# Revit family: NBS_HeatraeSadia_DrctHotWtrStrgCylndrsDblFeed_MEGAFLOEcoSolarReadyDirect
name_source: partatom
category: Mechanical Equipment
revit_build: Autodesk Revit 2014 (Build: 20130709_2115(x64)
units: mm (PartAtom-declared; Revit-internal decimal feet)

## types (1)
- 260DD
    AssetType = Fixed
    BIMObjectName = NBS_HeatraeSadia_IndirectHotWaterStorageCylindersDoubleFeed_MEGAFLOEcoSolarReady-260DD
    BackUpElementControlHousingHeight = 1165 mm
    Color = White
    Connections = 22 mm compression fittings
    ControlHousingMaterial = NBS_Concept
    CylinderMaterial = NBS_Concept
    Description = Unvented direct hot water cylinder
    DurationUnit = year
    EffectiveCapacity = 0 m³
    ElectricalDeviceNominalPower = 0
    ElementControlHousingHeight = 916 mm  [stored 3.00525 ft]
    ErPRating = C
    Features = Extrernal expansion vessel, specially designed solar coil for maximum effeciency, sized to deliver hot water even when solar gain is low,
    FirstCurvatureRadius = 0 mm  [stored 0 ft]
    Fixing = Floor fixed
    FlowRate = ≤70 L/min
    HasProtectiveEarth = No
    HeatUpTime = 60 minutes (minimum)
    Height = 1798 mm  [stored 5.89895 ft]
    IfcExportAs = IfcTankType
    IfcExportType = STORAGE
    ImmersionHeater = Two 3 kW titanium elements with integral thermostat and thermal cut-out
    ManufacturerName = Heatrae Sadia
    ManufacturerURL = www.heatraesadia.com
    Material = Outer casing: Plastic-coated corrosion-proofed steel; Water container: Duplex stainless steel
    MaterialThickness = 0 mm  [stored 0 ft]
    ModelNumber = 95:050:508
    ModelReference = MEGAFLO Eco SolarReady - 260DD
    NBSCertification = http://www.nationalbimlibrary.com
    NBSDescription = Indirect hot water storage cylinders, double feed
    NBSReference = 90-15-35/350
    Name = IndirectHotWaterStorageCylindersDoubleFeed_MEGAFLOEcoSolarReady-260DD_HeatraeSadia
    NominalCapacity = 7.36 m³
    NominalCurrent = 0
    NominalDepth = 1909 mm
    NominalFrequencyRange = 50.0, 60.0
    NominalLengthOrDiameter = 579 mm
    NominalVoltage = 230.0, 240.0
    NominalWidthOrDiameter = 579 mm
    NumberOfPoles = 0
    OperatingWeight = 307.3
    OutletTemperatureRange = ≤60°C
    PatternType = Vertical cylinder
    PhaseAngle = 0.00°
    ProductInformation = www.heatraesadia.com/docs/Megaflo_Eco_SolaReady_Technical_Data.pdf
    SafetyFeatures = Manually resettable thermal cutout on electrical supply to solar differential controller, manually resettable cut-out on each heating element set to operate at 85°C, temperature and pressure relief valve factory set to operate at 10 bar and 90°C, factory-fitted thermal cut-out for integration into a solar circuit
    SecondCurvatureRadius = 0 mm  [stored 0 ft]
    Shape = Cylinder
    Size = 1909 x 780 x 780 mm
    SolarCoilSurfaceArea = 1.1 m²
    SolarCoilType = 25 mm diameter stainless steel
    SupplyPressureRange = 1.5-16.0 bar
    ThermalInsulation = 60 mm thick CFC/HCFC free (ODP zero) fire retardant expanded polyurethane, foam
    ThirdPartyCertification = Kiwa approved, Nemko approved
    Uniclass2 = 90-90-87/423
    Uniclass2015Description = Double feed indirect hot water storage cylinders
    Uniclass2015Reference = Pr_60_50_20_23
    Uniclass2015Version = Products v1.1
    UsageCurrent = 0
    ValveMaterial = NBS_Concept
    Version = 1
    WarrantyDurationUnit = year
    WarrantyStartDate = 1900-12-31T23:59:59
    Width = 579 mm

note: [stored X ft] marks values corroborated as IEEE doubles in the binary element streams (Revit-internal decimal feet)

## geometry (parser evidence)
native form markers: Blend x14, Sweep x8
no freeform markers — native parametric forms only
